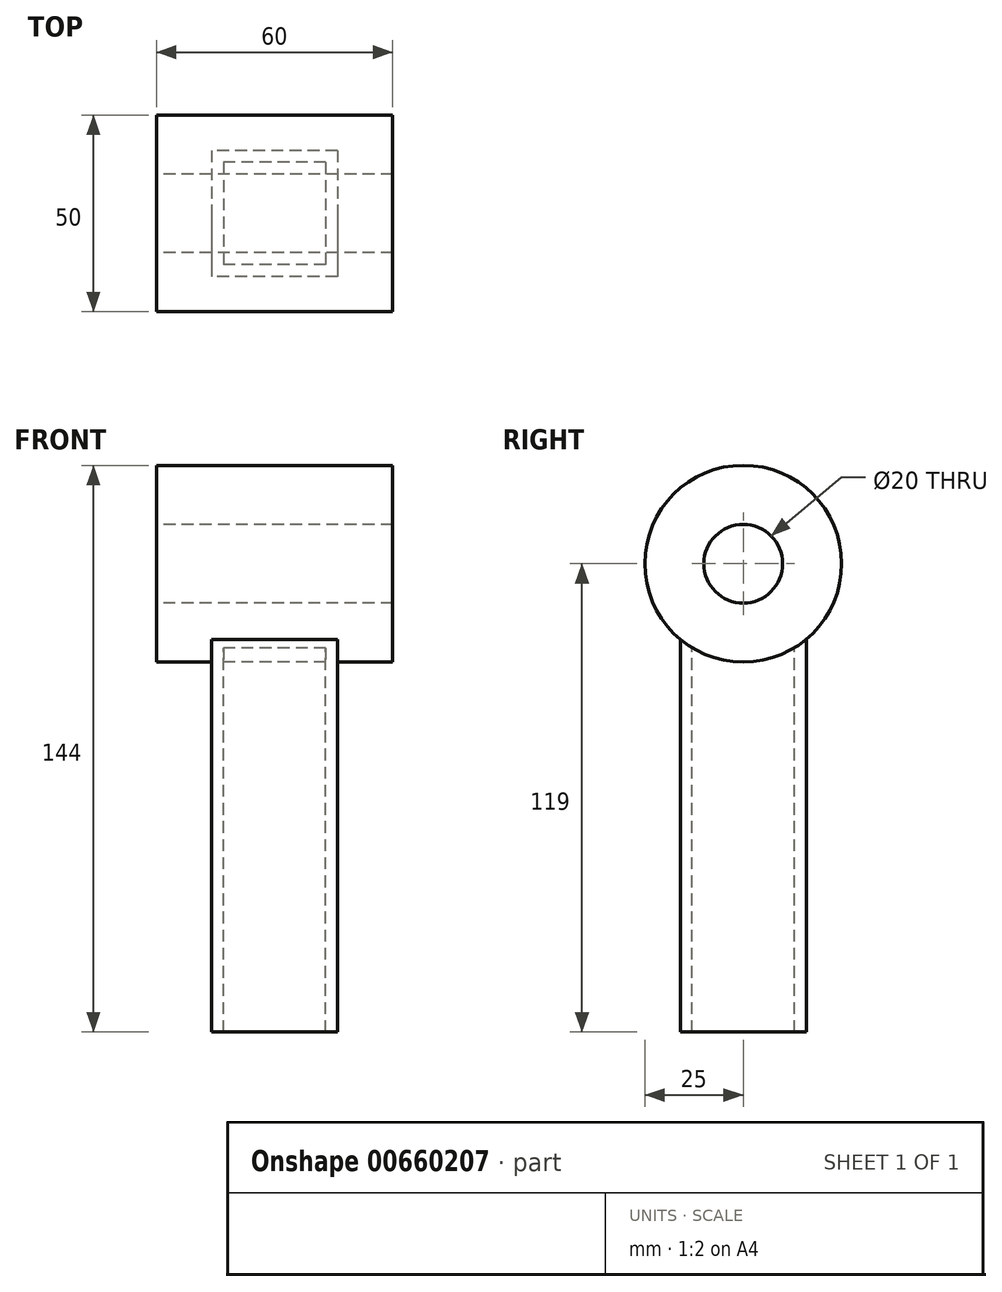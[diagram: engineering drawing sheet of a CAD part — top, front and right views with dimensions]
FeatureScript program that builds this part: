
annotation { "Feature Type Name" : "Feature", "Feature Type Description" : "" }
export const myFeature = defineFeature(function(context is Context, id is Id, definition is map)
    precondition{}
    {
        {
            var Q0;
            Q0=qCreatedBy(makeId("Top.planeOp"),FACE);
            var sketch = newSketch(context, id + "F0", { "sketchPlane" : qUnion([Q0])});
            skLineSegment(sketch, "E0.bottom", {"start": v(-16, 16) * mm, "end": v(16, 16) * mm});
            skLineSegment(sketch, "E0.top", {"start": v(-16, -16) * mm, "end": v(16, -16) * mm});
            skLineSegment(sketch, "E0.left", {"start": v(-16, 16) * mm, "end": v(-16, -16) * mm});
            skLineSegment(sketch, "E0.right", {"start": v(16, 16) * mm, "end": v(16, -16) * mm});
            skLineSegment(sketch, "E1.bottom", {"start": v(-13, 13) * mm, "end": v(13, 13) * mm});
            skLineSegment(sketch, "E1.top", {"start": v(-13, -13) * mm, "end": v(13, -13) * mm});
            skLineSegment(sketch, "E1.left", {"start": v(-13, 13) * mm, "end": v(-13, -13) * mm});
            skLineSegment(sketch, "E1.right", {"start": v(13, 13) * mm, "end": v(13, -13) * mm});
            skSolve(sketch);
        }
        {
            var Q0;
            Q0 = qSketchRegion(id + "F0", true);
            extrude(context, id + "F1", {"entities" : qUnion([Q0]), "oppositeDirection" : true, "depth" : 100 * mm, "offsetDistance" : 25 * mm});
        }
        {
            var Q0;
            Q0=qCreatedBy(makeId("Right.planeOp"),FACE);
            var sketch = newSketch(context, id + "F2", { "sketchPlane" : qUnion([Q0])});
            skCircle(sketch, "E2", {"center": v(0, 19) * mm, "radius": 25 * mm});
            skCircle(sketch, "E3", {"center": v(0, 19) * mm, "radius": 10 * mm});
            skSolve(sketch);
        }
        {
            var Q0;
            Q0 = qSketchRegion(id + "F2", true);
            extrude(context, id + "F3", {"entities" : qUnion([Q0]), "operationType" : NewBodyOperationType.ADD, "endBound" : BoundingType.SYMMETRIC, "depth" : 60 * mm, "offsetDistance" : 25 * mm});
        }
    });
